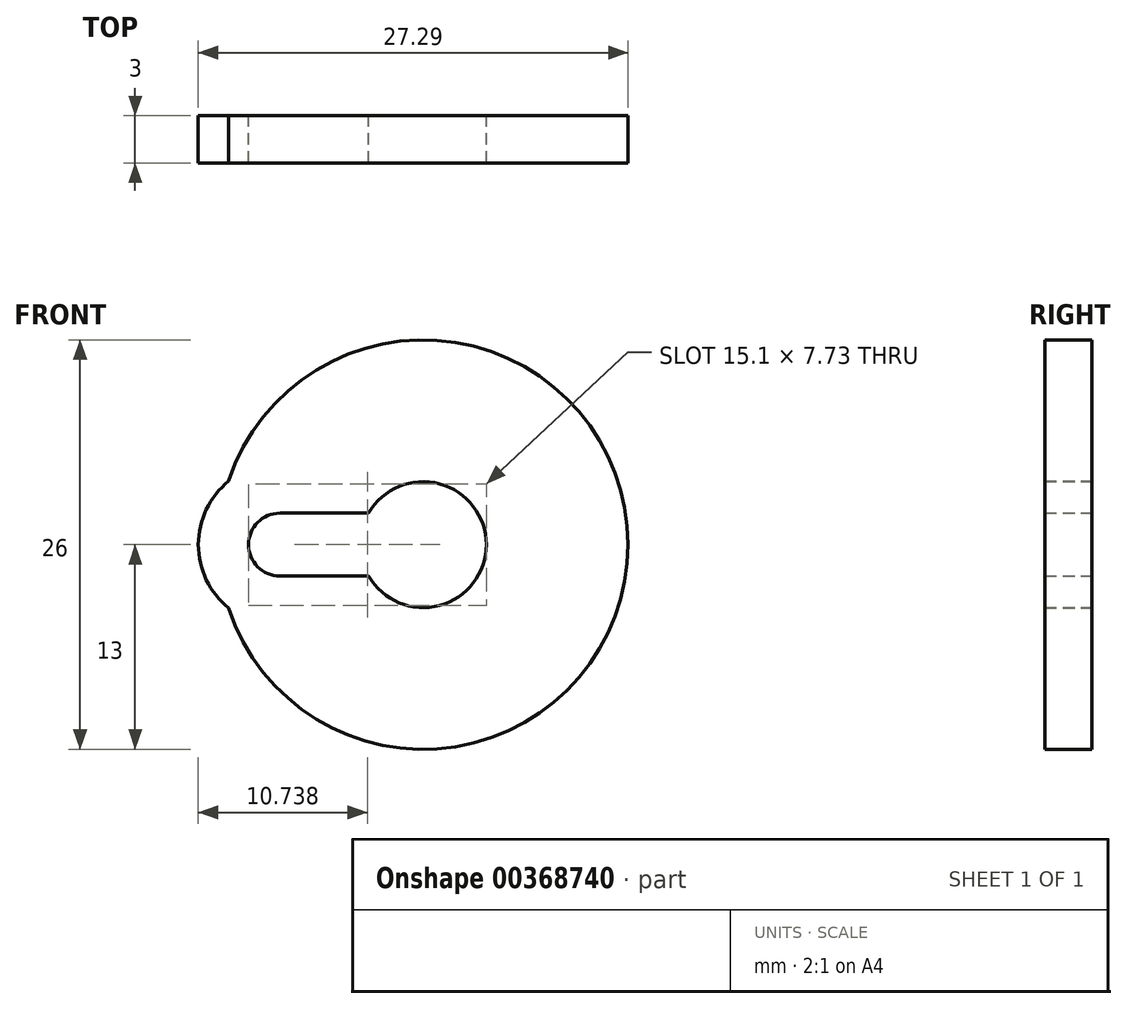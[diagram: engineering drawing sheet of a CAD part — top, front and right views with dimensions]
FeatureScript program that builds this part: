
annotation { "Feature Type Name" : "Feature", "Feature Type Description" : "" }
export const myFeature = defineFeature(function(context is Context, id is Id, definition is map)
    precondition{}
    {
        {
            var Q0;
            Q0=qCreatedBy(makeId("Front.planeOp"),FACE);
            var sketch = newSketch(context, id + "F0", { "sketchPlane" : qUnion([Q0])});
            skCircle(sketch, "E0", {"center": v(0, 0) * mm, "radius": 4 * mm});
            skCircle(sketch, "E1", {"center": v(0, 0) * mm, "radius": 13 * mm});
            skLineSegment(sketch, "E2.bottom", {"start": v(-9.1, 2) * mm, "end": v(-0.9, 2) * mm});
            skLineSegment(sketch, "E2.top", {"start": v(-9.1, -2) * mm, "end": v(-0.9, -2) * mm});
            skLineSegment(sketch, "E2.left", {"start": v(-9.1, 2) * mm, "end": v(-9.1, -2) * mm, "construction": true});
            skLineSegment(sketch, "E2.right", {"start": v(-0.9, 2) * mm, "end": v(-0.9, -2) * mm});
            skLineSegment(sketch, "E3", {"start": v(-9.1, 0) * mm, "end": v(0, 0) * mm, "construction": true});
            skCircle(sketch, "E4", {"center": v(-9.1, 0) * mm, "radius": 2 * mm});
            skCircle(sketch, "E5", {"center": v(-9.1, 0) * mm, "radius": 5.18 * mm});
            skSolve(sketch);
        }
        {
            var Q0;
            Q0=makeQuery(id+"F0.imprint","IMPRINT",FACE,{"disambiguationData":[TD([[makeQuery(id+"F0.imprint","IMPRINT",EDGE,{"derivedFrom":sQuery(id+"F0.wireOp",EDGE,"E1")}),1.0]])]});
            var Q1;
            {var subQ0=sQuery(id+"F0.wireOp",EDGE,"E5");var subQ1=sQuery(id+"F0.wireOp",EDGE,"E1");var subQ2=makeQuery(id+"F0.imprint","INTERSECT",VERTEX,{"disambiguationData":[OD(0.0)],"derivedFrom":[subQ1,subQ0]});Q1=makeQuery(id+"F0.imprint","IMPRINT",FACE,{"disambiguationData":[TD([[makeQuery(id+"F0.imprint","IMPRINT",EDGE,{"disambiguationData":[TD([[subQ2,-1.0]])],"derivedFrom":subQ1}),-1.0]])]});}
            extrude(context, id + "F1", {"entities" : qUnion([Q0, Q1]), "depth" : 3 * mm});
        }
    });
